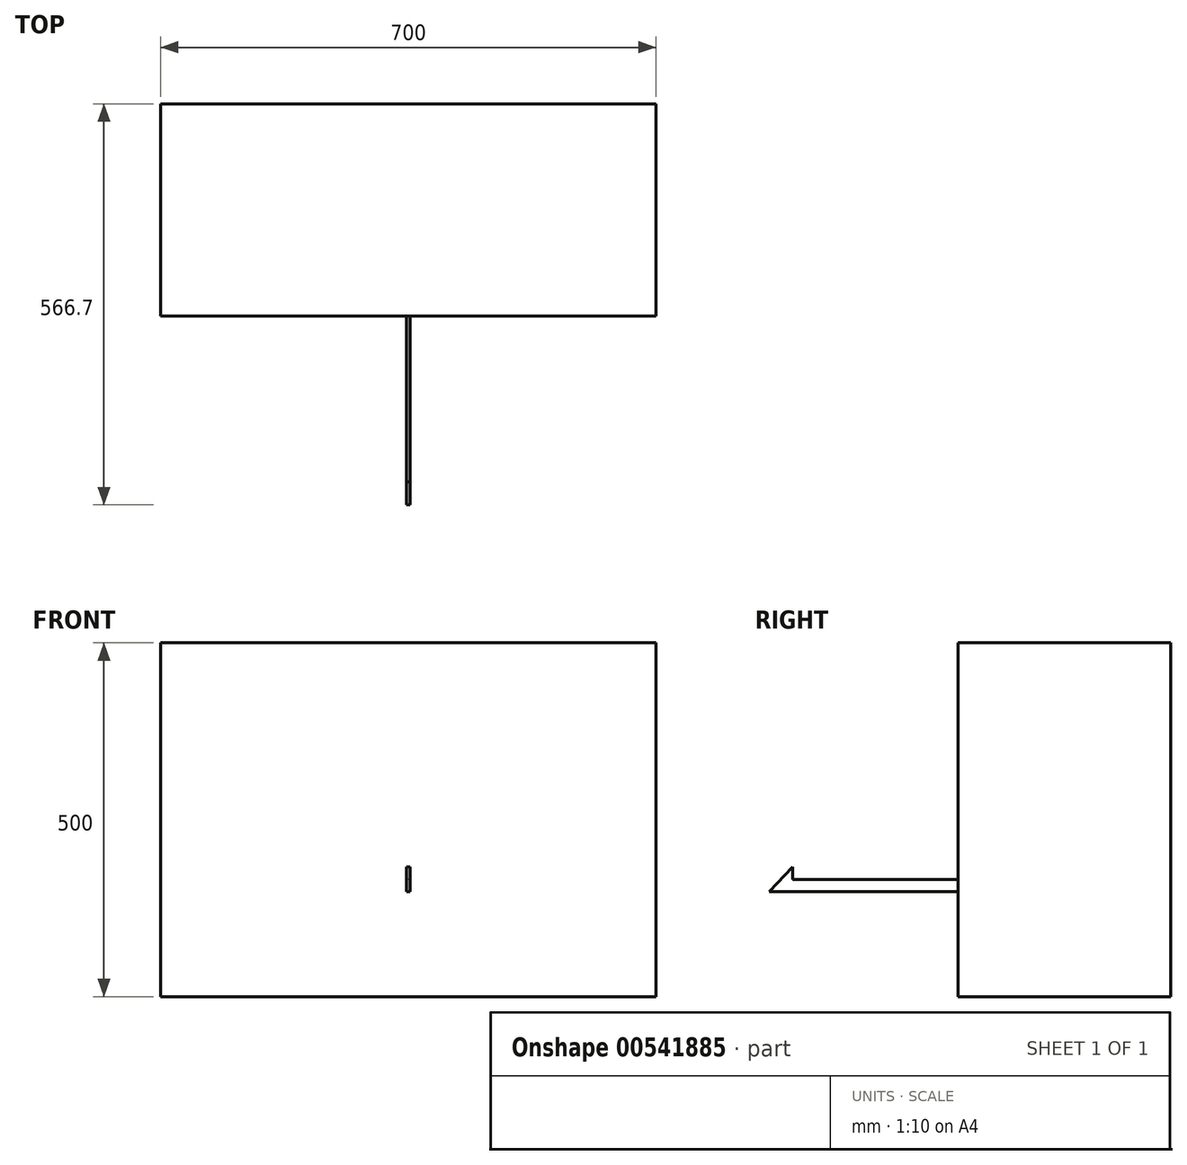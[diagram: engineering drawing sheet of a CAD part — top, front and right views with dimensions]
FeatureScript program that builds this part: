
annotation { "Feature Type Name" : "Feature", "Feature Type Description" : "" }
export const myFeature = defineFeature(function(context is Context, id is Id, definition is map)
    precondition{}
    {
        {
            var Q0;
            Q0=qCreatedBy(makeId("Front.planeOp"),FACE);
            var sketch = newSketch(context, id + "F0", { "sketchPlane" : qUnion([Q0])});
            skLineSegment(sketch, "E0.bottom", {"start": v(-700, 0) * mm, "end": v(0, 0) * mm});
            skLineSegment(sketch, "E0.top", {"start": v(-700, -500) * mm, "end": v(0, -500) * mm});
            skLineSegment(sketch, "E0.left", {"start": v(-700, 0) * mm, "end": v(-700, -500) * mm});
            skLineSegment(sketch, "E0.right", {"start": v(0, 0) * mm, "end": v(0, -500) * mm});
            skSolve(sketch);
        }
        {
            var Q0;
            Q0=makeQuery(id+"F0.imprint","IMPRINT",FACE,{"disambiguationData":[TD([[makeQuery(id+"F0.imprint","IMPRINT",EDGE,{"derivedFrom":sQuery(id+"F0.wireOp",EDGE,"E0.bottom")}),-1.0]])]});
            extrude(context, id + "F1", {"entities" : qUnion([Q0]), "depth" : 300 * mm, "offsetDistance" : 25.4 * mm});
        }
        {
            var Q0;
            Q0=makeQuery(id+"F1.opExtrude","CAP_FACE",FACE,{"disambiguationData":[OSD([sQuery(id+"F0.wireOp",EDGE,"E0.bottom"),sQuery(id+"F0.wireOp",EDGE,"E0.top"),sQuery(id+"F0.wireOp",EDGE,"E0.left"),sQuery(id+"F0.wireOp",EDGE,"E0.right")])],"isStart":false});
            var sketch = newSketch(context, id + "F2", { "sketchPlane" : qUnion([Q0])});
            skLineSegment(sketch, "E1.bottom", {"start": v(-352.5, -351.74) * mm, "end": v(-347.5, -351.74) * mm});
            skLineSegment(sketch, "E1.top", {"start": v(-352.5, -316.84) * mm, "end": v(-347.5, -316.84) * mm});
            skLineSegment(sketch, "E1.left", {"start": v(-352.5, -351.74) * mm, "end": v(-352.5, -316.84) * mm});
            skLineSegment(sketch, "E1.right", {"start": v(-347.5, -351.74) * mm, "end": v(-347.5, -316.84) * mm});
            skSolve(sketch);
        }
        {
            var Q0;
            Q0=makeQuery(id+"F2.imprint","IMPRINT",FACE,{"disambiguationData":[TD([[makeQuery(id+"F2.imprint","IMPRINT",EDGE,{"derivedFrom":sQuery(id+"F2.wireOp",EDGE,"E1.bottom")}),1.0]])]});
            extrude(context, id + "F3", {"entities" : qUnion([Q0]), "operationType" : NewBodyOperationType.ADD, "depth" : 266.7 * mm, "offsetDistance" : 25.4 * mm});
        }
        {
            var Q0;
            Q0=makeQuery(id+"F3.opExtrude","SWEPT_FACE",FACE,{"disambiguationData":[OSD([sQuery(id+"F2.wireOp",EDGE,"E1.left")])]});
            var sketch = newSketch(context, id + "F4", { "sketchPlane" : qUnion([Q0])});
            skLineSegment(sketch, "E2", {"start": v(566.7, -351.74) * mm, "end": v(533.93, -316.84) * mm});
            skLineSegment(sketch, "E3", {"start": v(533.93, -316.84) * mm, "end": v(533.93, -334.29) * mm});
            skLineSegment(sketch, "E4", {"start": v(533.93, -334.29) * mm, "end": v(300, -334.29) * mm});
            skLineSegment(sketch, "E5", {"start": v(566.7, -351.74) * mm, "end": v(566.7, -316.84) * mm});
            skLineSegment(sketch, "E6", {"start": v(566.7, -316.84) * mm, "end": v(533.93, -316.84) * mm});
            skLineSegment(sketch, "E7", {"start": v(300, -316.84) * mm, "end": v(300, -334.29) * mm});
            skLineSegment(sketch, "E8", {"start": v(533.93, -316.84) * mm, "end": v(300, -316.84) * mm});
            skSolve(sketch);
        }
        {
            var Q0;
            Q0 = qSketchRegion(id + "F4", true);
            extrude(context, id + "F5", {"entities" : qUnion([Q0]), "operationType" : NewBodyOperationType.REMOVE, "oppositeDirection" : true, "depth" : 25.4 * mm, "offsetDistance" : 25.4 * mm});
        }
    });
